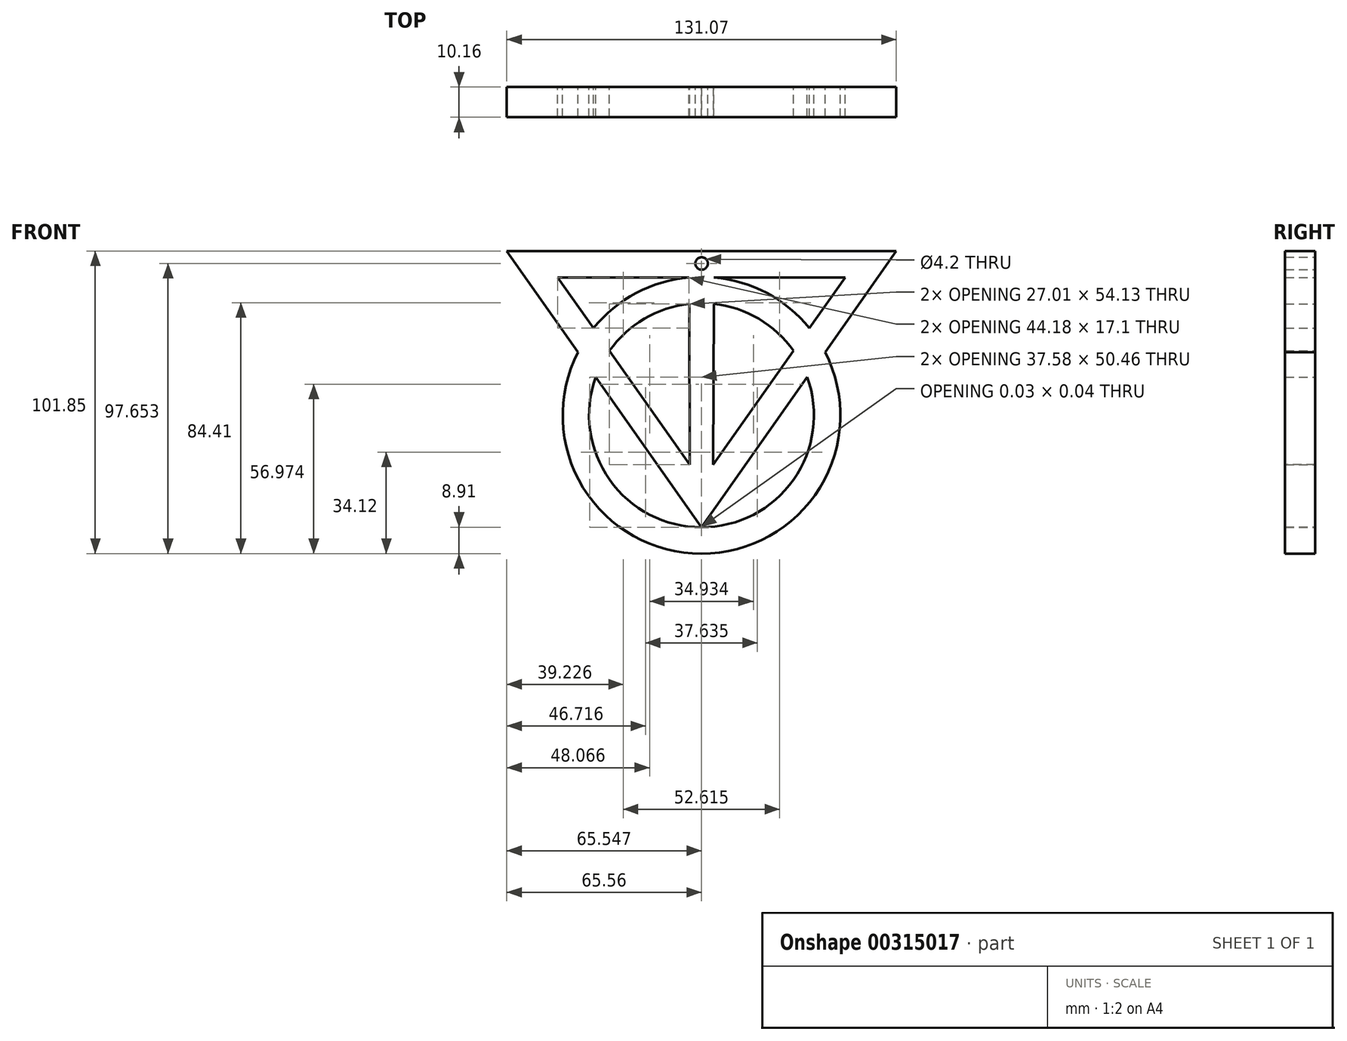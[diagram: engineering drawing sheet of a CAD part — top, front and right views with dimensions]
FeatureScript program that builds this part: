
annotation { "Feature Type Name" : "Feature", "Feature Type Description" : "" }
export const myFeature = defineFeature(function(context is Context, id is Id, definition is map)
    precondition{}
    {
        {
            var Q0;
            Q0=qCreatedBy(makeId("Front.planeOp"),FACE);
            var sketch = newSketch(context, id + "F0", { "sketchPlane" : qUnion([Q0])});
            skLineSegment(sketch, "E0", {"start": v(0, -37.68) * mm, "end": v(-0.03, -37.64) * mm});
            skPoint(sketch, "E1.orphan", {"position": v(-128.31, 0) * mm});
            skPoint(sketch, "E2.orphan", {"position": v(-71.02, -128.9) * mm});
            skArc(sketch, "E3.trimOffspring", {"start": v(-3.65, 37.5) * mm, "mid": v(-3.9, 37.46) * mm, "end": v(-4.15, 37.44) * mm});
            skLineSegment(sketch, "E4.0", {"start": v(-3.8, -16.64) * mm, "end": v(-4, -16.38) * mm});
            skPoint(sketch, "E5.end.orphan", {"position": v(-123.71, -191.43) * mm});
            skLineSegment(sketch, "E6.MirrorCS", {"start": v(0, -37.68) * mm, "end": v(35.56, 12.78) * mm});
            skLineSegment(sketch, "E7.MirrorCS", {"start": v(30.94, 21.66) * mm, "end": v(30.94, 21.66) * mm});
            skLineSegment(sketch, "E8.MirrorCS", {"start": v(36.32, 29.29) * mm, "end": v(48.37, 46.4) * mm});
            skLineSegment(sketch, "E9.trimOffspring", {"start": v(3.94, -16.66) * mm, "end": v(30.94, 21.66) * mm});
            skPoint(sketch, "E10.orphan", {"position": v(0.05, -22.18) * mm});
            skArc(sketch, "E11.trimOffspring", {"start": v(35.56, 12.78) * mm, "mid": v(30.91, -21.7) * mm, "end": v(0, -37.68) * mm});
            skArc(sketch, "E12.trimOffspring", {"start": v(-0.05, -37.68) * mm, "mid": v(-0.03, -37.68) * mm, "end": v(0, -37.68) * mm});
            skArc(sketch, "E13.0", {"start": v(-0.06, -46.57) * mm, "mid": v(-0.04, -46.57) * mm, "end": v(-0.03, -46.57) * mm});
            skArc(sketch, "E14.0", {"start": v(41.54, 21.27) * mm, "mid": v(39.82, -24.33) * mm, "end": v(-0.03, -46.57) * mm});
            skArc(sketch, "E15.0", {"start": v(4.2, 46.4) * mm, "mid": v(22, 41.1) * mm, "end": v(36.32, 29.29) * mm});
            skPoint(sketch, "E16.center.orphan", {"position": v(0, 42.2) * mm});
            skLineSegment(sketch, "E17", {"start": v(48.37, 46.4) * mm, "end": v(4.2, 46.4) * mm});
            skLineSegment(sketch, "E18.0", {"start": v(65.51, 55.28) * mm, "end": v(-0.03, 55.28) * mm});
            skArc(sketch, "E19.0", {"start": v(4.1, 37.47) * mm, "mid": v(19.23, 32.47) * mm, "end": v(30.94, 21.66) * mm});
            skLineSegment(sketch, "E20", {"start": v(3.94, -16.66) * mm, "end": v(4.1, 37.47) * mm});
            skLineSegment(sketch, "E21.trimOffspring", {"start": v(41.54, 21.27) * mm, "end": v(65.51, 55.28) * mm});
            skLineSegment(sketch, "E22.trimOffspring", {"start": v(-3.96, 46.4) * mm, "end": v(-4.24, 46.4) * mm});
            skLineSegment(sketch, "E23", {"start": v(-0.03, -37.68) * mm, "end": v(-0.03, -37.64) * mm});
            skLineSegment(sketch, "E24.MirrorCS", {"start": v(-48.42, 46.4) * mm, "end": v(-47.66, 46.4) * mm});
            skLineSegment(sketch, "E25.MirrorCS", {"start": v(-4, -16.66) * mm, "end": v(-4, -16.38) * mm});
            skLineSegment(sketch, "E26.trimOffspring", {"start": v(-0.03, 55.28) * mm, "end": v(64.62, 55.28) * mm});
            skPoint(sketch, "E27.MirrorCS.end.orphan", {"position": v(-4, -16.66) * mm});
            skPoint(sketch, "E27.MirrorCS.start.orphan", {"position": v(-31, 21.66) * mm});
            skPoint(sketch, "E28.MirrorCS.end.orphan", {"position": v(-65.56, 55.28) * mm});
            skPoint(sketch, "E28.MirrorCS.start.orphan", {"position": v(-41.6, 21.27) * mm});
            skPoint(sketch, "E29.MirrorCS.end.orphan", {"position": v(-64.67, 55.28) * mm});
            skPoint(sketch, "E30.orphan", {"position": v(-4.24, 46.4) * mm});
            skPoint(sketch, "E31.MirrorCS.start.orphan", {"position": v(-4.15, 37.47) * mm});
            skPoint(sketch, "E32.MirrorCS.start.orphan", {"position": v(-35.61, 12.78) * mm});
            skLineSegment(sketch, "E33.trimOffspring", {"start": v(-4.15, 37.44) * mm, "end": v(-4.15, 37.47) * mm});
            skArc(sketch, "E34.MirrorCS", {"start": v(-35.61, 12.78) * mm, "mid": v(-30.97, -21.7) * mm, "end": v(-0.05, -37.68) * mm});
            skLineSegment(sketch, "E35.MirrorCS", {"start": v(-0.05, -37.68) * mm, "end": v(-35.61, 12.78) * mm});
            skArc(sketch, "E36.MirrorCS", {"start": v(-41.6, 21.27) * mm, "mid": v(-39.87, -24.33) * mm, "end": v(-0.03, -46.57) * mm});
            skLineSegment(sketch, "E37.MirrorCS", {"start": v(-4, -16.66) * mm, "end": v(-31, 21.66) * mm});
            skArc(sketch, "E38.MirrorCS", {"start": v(-4.15, 37.47) * mm, "mid": v(-19.29, 32.47) * mm, "end": v(-31, 21.66) * mm});
            skLineSegment(sketch, "E39.MirrorCS", {"start": v(-4, -16.66) * mm, "end": v(-4.15, 37.47) * mm});
            skArc(sketch, "E40.MirrorCS", {"start": v(-4.24, 46.4) * mm, "mid": v(-22.05, 41.1) * mm, "end": v(-36.37, 29.29) * mm});
            skLineSegment(sketch, "E41.MirrorCS", {"start": v(-0.03, 55.28) * mm, "end": v(-65.56, 55.28) * mm});
            skLineSegment(sketch, "E42.MirrorCS", {"start": v(-41.6, 21.27) * mm, "end": v(-65.56, 55.28) * mm});
            skLineSegment(sketch, "E43.MirrorCS", {"start": v(-48.42, 46.4) * mm, "end": v(-4.24, 46.4) * mm});
            skLineSegment(sketch, "E44.MirrorCS", {"start": v(-36.37, 29.29) * mm, "end": v(-48.42, 46.4) * mm});
            skCircle(sketch, "E45", {"center": v(0, 51.08) * mm, "radius": 2.1 * mm});
            skSolve(sketch);
        }
        {
            var Q0;
            {var subQ13=sQuery(id+"F0.wireOp",EDGE,"E0");Q0=makeQuery(id+"F0.imprint","IMPRINT",FACE,{"disambiguationData":[TD([[makeQuery(id+"F0.imprint","IMPRINT",EDGE,{"derivedFrom":subQ13}),-1.0]])]});}
            extrude(context, id + "F1", {"entities" : qUnion([Q0]), "depth" : 10.16 * mm});
        }
    });
